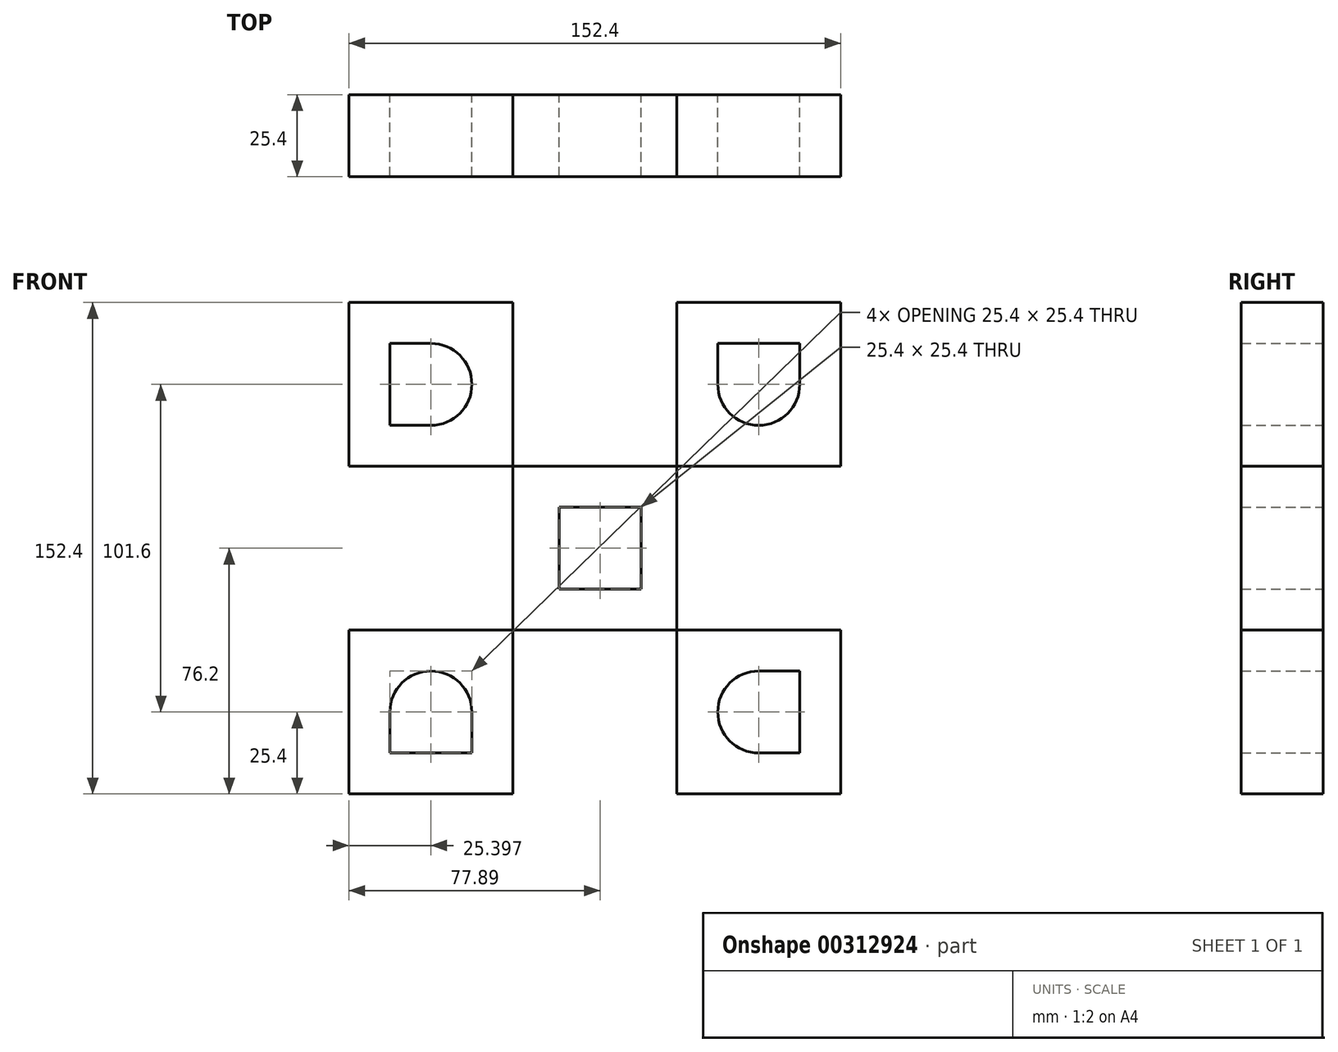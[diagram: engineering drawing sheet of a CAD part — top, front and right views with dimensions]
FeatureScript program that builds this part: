
annotation { "Feature Type Name" : "Feature", "Feature Type Description" : "" }
export const myFeature = defineFeature(function(context is Context, id is Id, definition is map)
    precondition{}
    {
        {
            var Q0;
            Q0=qCreatedBy(makeId("Front.planeOp"),FACE);
            var sketch = newSketch(context, id + "F0", { "sketchPlane" : qUnion([Q0])});
            skLineSegment(sketch, "E0.bottom", {"start": v(23.7, 25.4) * mm, "end": v(-27.1, 25.4) * mm});
            skLineSegment(sketch, "E0.top", {"start": v(23.7, -25.4) * mm, "end": v(-27.1, -25.4) * mm});
            skLineSegment(sketch, "E0.left", {"start": v(23.7, 25.4) * mm, "end": v(23.7, -25.4) * mm});
            skLineSegment(sketch, "E0.right", {"start": v(-27.1, 25.4) * mm, "end": v(-27.1, -25.4) * mm});
            skLineSegment(sketch, "E1.bottom", {"start": v(-27.1, -25.4) * mm, "end": v(-77.9, -25.4) * mm});
            skLineSegment(sketch, "E1.top", {"start": v(-27.1, -76.2) * mm, "end": v(-77.9, -76.2) * mm});
            skLineSegment(sketch, "E1.left", {"start": v(-27.1, -25.4) * mm, "end": v(-27.1, -76.2) * mm});
            skLineSegment(sketch, "E1.right", {"start": v(-77.9, -25.4) * mm, "end": v(-77.9, -76.2) * mm});
            skLineSegment(sketch, "E2.bottom", {"start": v(23.7, -25.4) * mm, "end": v(74.5, -25.4) * mm});
            skLineSegment(sketch, "E2.top", {"start": v(23.7, -76.2) * mm, "end": v(74.5, -76.2) * mm});
            skLineSegment(sketch, "E2.left", {"start": v(23.7, -25.4) * mm, "end": v(23.7, -76.2) * mm});
            skLineSegment(sketch, "E2.right", {"start": v(74.5, -25.4) * mm, "end": v(74.5, -76.2) * mm});
            skLineSegment(sketch, "E3.bottom", {"start": v(23.7, 25.4) * mm, "end": v(74.5, 25.4) * mm});
            skLineSegment(sketch, "E3.top", {"start": v(23.7, 76.2) * mm, "end": v(74.5, 76.2) * mm});
            skLineSegment(sketch, "E3.left", {"start": v(23.7, 25.4) * mm, "end": v(23.7, 76.2) * mm});
            skLineSegment(sketch, "E3.right", {"start": v(74.5, 25.4) * mm, "end": v(74.5, 76.2) * mm});
            skLineSegment(sketch, "E4.bottom", {"start": v(-27.1, 25.4) * mm, "end": v(-77.9, 25.4) * mm});
            skLineSegment(sketch, "E4.top", {"start": v(-27.1, 76.2) * mm, "end": v(-77.9, 76.2) * mm});
            skLineSegment(sketch, "E4.left", {"start": v(-27.1, 25.4) * mm, "end": v(-27.1, 76.2) * mm});
            skLineSegment(sketch, "E4.right", {"start": v(-77.9, 25.4) * mm, "end": v(-77.9, 76.2) * mm});
            skLineSegment(sketch, "E5.bottom", {"start": v(-52.5, 38.1) * mm, "end": v(-65.2, 38.1) * mm});
            skLineSegment(sketch, "E5.top", {"start": v(-52.5, 63.5) * mm, "end": v(-65.2, 63.5) * mm});
            skLineSegment(sketch, "E5.right", {"start": v(-65.2, 38.1) * mm, "end": v(-65.2, 63.5) * mm});
            skPoint(sketch, "E5.middle", {"position": v(-52.5, 50.8) * mm});
            skPoint(sketch, "E5.middle.positionSnap0", {"position": v(-27.1, 50.8) * mm});
            skPoint(sketch, "E5.middle.positionSnap1", {"position": v(-52.5, 76.2) * mm});
            skPoint(sketch, "E5.centerSnap0", {"position": v(-27.1, 50.8) * mm});
            skPoint(sketch, "E5.centerSnap1", {"position": v(-52.5, 76.2) * mm});
            skLineSegment(sketch, "E6.bottom", {"start": v(49.1, 55.82) * mm, "end": v(49.1, 55.82) * mm});
            skLineSegment(sketch, "E6.top", {"start": v(49.1, 96.58) * mm, "end": v(49.1, 96.58) * mm});
            skPoint(sketch, "E6.middle", {"position": v(49.1, 76.2) * mm});
            skPoint(sketch, "E6.cornerSnap0", {"position": v(49.1, 76.2) * mm});
            skLineSegment(sketch, "E7.top", {"start": v(61.8, 63.5) * mm, "end": v(36.4, 63.5) * mm});
            skLineSegment(sketch, "E7.left", {"start": v(61.8, 50.8) * mm, "end": v(61.8, 63.5) * mm});
            skLineSegment(sketch, "E7.right", {"start": v(36.4, 50.8) * mm, "end": v(36.4, 63.5) * mm});
            skPoint(sketch, "E7.middle", {"position": v(49.1, 50.8) * mm});
            skPoint(sketch, "E7.middle.positionSnap0", {"position": v(49.1, 25.4) * mm});
            skPoint(sketch, "E7.middle.positionSnap1", {"position": v(74.5, 50.8) * mm});
            skPoint(sketch, "E7.centerSnap0", {"position": v(49.1, 25.4) * mm});
            skPoint(sketch, "E7.centerSnap1", {"position": v(74.5, 50.8) * mm});
            skLineSegment(sketch, "E8.top", {"start": v(-39.8, -63.5) * mm, "end": v(-52.5, -63.5) * mm});
            skLineSegment(sketch, "E8.left", {"start": v(-39.8, -50.8) * mm, "end": v(-39.8, -63.5) * mm});
            skPoint(sketch, "E8.middle", {"position": v(-52.5, -50.8) * mm});
            skPoint(sketch, "E8.middle.positionSnap0", {"position": v(-52.5, -76.2) * mm});
            skPoint(sketch, "E8.middle.positionSnap1", {"position": v(-27.1, -50.8) * mm});
            skPoint(sketch, "E8.centerSnap0", {"position": v(-52.5, -76.2) * mm});
            skPoint(sketch, "E8.centerSnap1", {"position": v(-27.1, -50.8) * mm});
            skLineSegment(sketch, "E9.bottom", {"start": v(49.1, -38.1) * mm, "end": v(61.8, -38.1) * mm});
            skLineSegment(sketch, "E9.top", {"start": v(49.1, -63.5) * mm, "end": v(61.8, -63.5) * mm});
            skLineSegment(sketch, "E9.right", {"start": v(61.8, -38.1) * mm, "end": v(61.8, -63.5) * mm});
            skPoint(sketch, "E9.middle", {"position": v(49.1, -50.8) * mm});
            skPoint(sketch, "E9.middle.positionSnap0", {"position": v(49.1, -76.2) * mm});
            skPoint(sketch, "E9.middle.positionSnap1", {"position": v(74.5, -50.8) * mm});
            skPoint(sketch, "E9.centerSnap0", {"position": v(49.1, -76.2) * mm});
            skPoint(sketch, "E9.centerSnap1", {"position": v(74.5, -50.8) * mm});
            skPoint(sketch, "E10.middle.positionSnap0", {"position": v(-1.7, -25.4) * mm});
            skPoint(sketch, "E10.centerSnap0", {"position": v(-1.7, -25.4) * mm});
            skCircle(sketch, "E11", {"center": v(-52.5, 50.8) * mm, "radius": 12.7 * mm});
            skCircle(sketch, "E12", {"center": v(49.1, 50.8) * mm, "radius": 12.7 * mm});
            skCircle(sketch, "E13", {"center": v(-52.5, -50.8) * mm, "radius": 12.7 * mm});
            skCircle(sketch, "E14", {"center": v(49.1, -50.8) * mm, "radius": 12.7 * mm});
            skLineSegment(sketch, "E15.bottom", {"start": v(-12.7, 12.7) * mm, "end": v(12.7, 12.7) * mm});
            skLineSegment(sketch, "E15.top", {"start": v(-12.7, -12.7) * mm, "end": v(12.7, -12.7) * mm});
            skLineSegment(sketch, "E15.left", {"start": v(-12.7, 12.7) * mm, "end": v(-12.7, -12.7) * mm});
            skLineSegment(sketch, "E15.right", {"start": v(12.7, 12.7) * mm, "end": v(12.7, -12.7) * mm});
            skPoint(sketch, "E15.middle", {"position": v(0, 0) * mm});
            skCircle(sketch, "E16", {"center": v(0, 0) * mm, "radius": 12.7 * mm});
            skPoint(sketch, "E17.orphan", {"position": v(36.4, 38.1) * mm});
            skPoint(sketch, "E18.orphan", {"position": v(61.8, 38.1) * mm});
            skPoint(sketch, "E19.orphan", {"position": v(36.4, -38.1) * mm});
            skPoint(sketch, "E20.orphan", {"position": v(36.4, -63.5) * mm});
            skPoint(sketch, "E21.orphan", {"position": v(-65.2, -38.1) * mm});
            skPoint(sketch, "E22.orphan", {"position": v(-39.8, -38.1) * mm});
            skPoint(sketch, "E23.orphan", {"position": v(-39.8, 63.5) * mm});
            skPoint(sketch, "E24.orphan", {"position": v(-39.8, 38.1) * mm});
            skPoint(sketch, "E25.orphan", {"position": v(-65.2, -63.5) * mm});
            skLineSegment(sketch, "E26.bottom", {"start": v(-39.8, -63.5) * mm, "end": v(-65.2, -63.5) * mm});
            skLineSegment(sketch, "E26.left", {"start": v(-39.8, -63.5) * mm, "end": v(-39.8, -50.8) * mm});
            skLineSegment(sketch, "E26.right", {"start": v(-65.2, -63.5) * mm, "end": v(-65.2, -50.8) * mm});
            skSolve(sketch);
        }
        {
            var Q0;
            Q0 = qSketchRegion(id + "F0", true);
            extrude(context, id + "F1", {"entities" : qUnion([Q0]), "depth" : 25.4 * mm});
        }
    });
